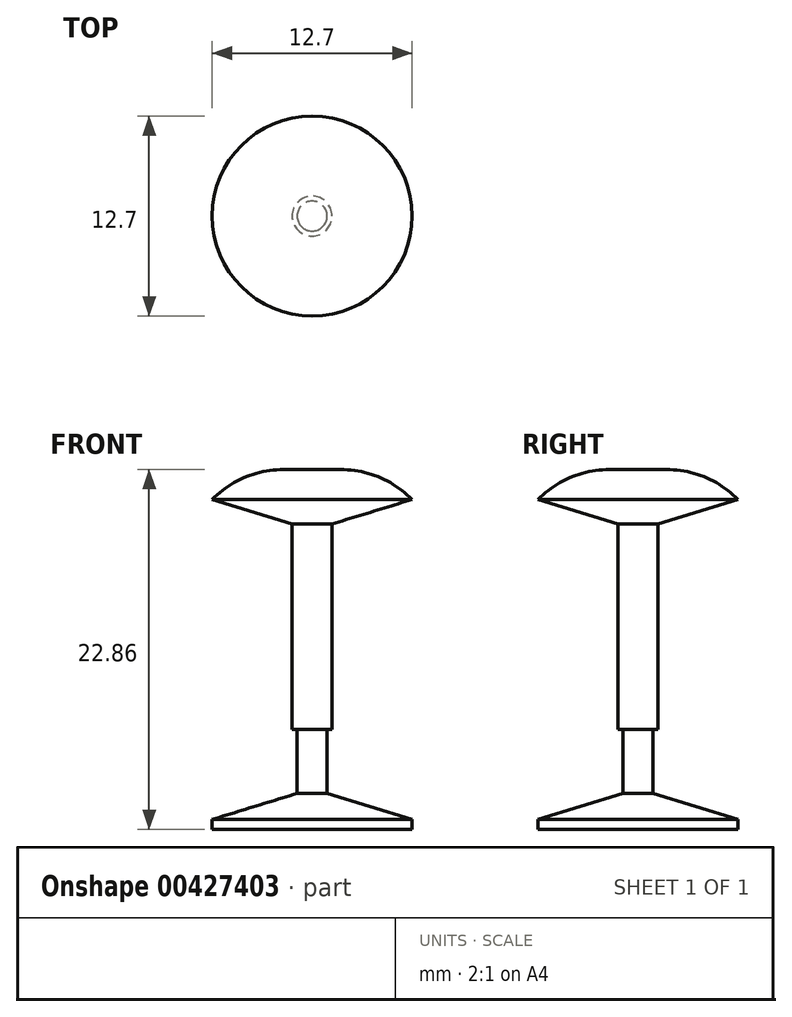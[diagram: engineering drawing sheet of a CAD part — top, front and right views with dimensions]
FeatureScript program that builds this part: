
annotation { "Feature Type Name" : "Feature", "Feature Type Description" : "" }
export const myFeature = defineFeature(function(context is Context, id is Id, definition is map)
    precondition{}
    {
        {
            var Q0;
            Q0=qCreatedBy(makeId("Top.planeOp"),FACE);
            var sketch = newSketch(context, id + "F0", { "sketchPlane" : qUnion([Q0])});
            skCircle(sketch, "E0", {"center": v(0, 0) * mm, "radius": 6.35 * mm});
            skSolve(sketch);
        }
        {
            var Q0;
            Q0 = qSketchRegion(id + "F0", true);
            extrude(context, id + "F1", {"entities" : qUnion([Q0]), "depth" : 2.54 * mm});
        }
        {
            var Q0;
            Q0=makeQuery(id+"F1.opExtrude","CAP_FACE",FACE,{"disambiguationData":[OSD([sQuery(id+"F0.wireOp",EDGE,"E0")])],"isStart":false});
            var sketch = newSketch(context, id + "F2", { "sketchPlane" : qUnion([Q0])});
            skCircle(sketch, "E1", {"center": v(0, 0) * mm, "radius": 0.95 * mm});
            skSolve(sketch);
        }
        {
            var Q0;
            Q0 = qSketchRegion(id + "F2", true);
            extrude(context, id + "F3", {"entities" : qUnion([Q0]), "operationType" : NewBodyOperationType.ADD, "depth" : 3.8 * mm});
        }
        {
            var Q0;
            Q0=makeQuery(id+"F3.opExtrude","CAP_FACE",FACE,{"disambiguationData":[OSD([sQuery(id+"F2.wireOp",EDGE,"E1")])],"isStart":false});
            var sketch = newSketch(context, id + "F4", { "sketchPlane" : qUnion([Q0])});
            skCircle(sketch, "E2", {"center": v(0, 0) * mm, "radius": 1.27 * mm});
            skSolve(sketch);
        }
        {
            var Q0;
            Q0 = qSketchRegion(id + "F4", true);
            extrude(context, id + "F5", {"entities" : qUnion([Q0]), "operationType" : NewBodyOperationType.ADD, "depth" : 12.7 * mm});
        }
        {
            var Q0;
            Q0=makeQuery(id+"F5.opExtrude","CAP_FACE",FACE,{"disambiguationData":[OSD([sQuery(id+"F4.wireOp",EDGE,"E2")])],"isStart":false});
            var sketch = newSketch(context, id + "F6", { "sketchPlane" : qUnion([Q0])});
            skCircle(sketch, "E3", {"center": v(0, 0) * mm, "radius": 6.35 * mm});
            skSolve(sketch);
        }
        {
            var Q0;
            Q0 = qSketchRegion(id + "F6", true);
            extrude(context, id + "F7", {"entities" : qUnion([Q0]), "operationType" : NewBodyOperationType.ADD, "depth" : 3.8 * mm});
        }
        {
            var Q0;
            Q0=makeQuery(id+"F1.opExtrude","CAP_EDGE",EDGE,{"disambiguationData":[OSD([sQuery(id+"F0.wireOp",EDGE,"E0")])],"isStart":false});
            chamfer(context, id + "F8", {"entities" : qUnion([Q0]), "chamferType" : ChamferType.OFFSET_ANGLE, "width" : 1.9 * mm, "oppositeDirection" : true, "angle" : 73 * degree, "tangentPropagation" : true});
        }
        {
            var Q0;
            Q0=makeQuery(id+"F7.opExtrude","CAP_EDGE",EDGE,{"disambiguationData":[OSD([sQuery(id+"F6.wireOp",EDGE,"E3")])],"isStart":true});
            chamfer(context, id + "F9", {"entities" : qUnion([Q0]), "chamferType" : ChamferType.OFFSET_ANGLE, "width" : 1.9 * mm, "oppositeDirection" : false, "angle" : 73 * degree, "tangentPropagation" : true});
        }
        {
            var Q0;
            Q0=makeQuery(id+"F7.opExtrude","CAP_EDGE",EDGE,{"disambiguationData":[OSD([sQuery(id+"F6.wireOp",EDGE,"E3")])],"isStart":false});
            fillet(context, id + "F10", {"entities" : qUnion([Q0]), "radius" : 6.35 * mm, "tangentPropagation" : true, "allowEdgeOverflow" : false});
        }
    });
